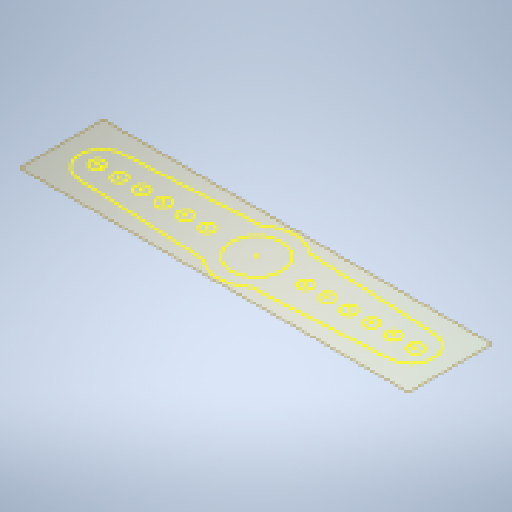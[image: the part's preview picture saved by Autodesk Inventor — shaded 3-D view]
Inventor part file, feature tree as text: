
AUTODESK INVENTOR PART (.ipt)
format: ipt  version: 2024 (Build 280153000, 153)  size: 168,960 bytes
history: native  units: mm
features: other x4, extrude x2, sketch x2, plane x1, reference x1
ambient origin geometry x8: Origin, YZ Plane, XZ Plane, XY Plane, X Axis, Y Axis, Z Axis, Center Point
bodies: Solid1 (feature_tree)
feature tree (10):
  plane  "Work Plane1"
  extrude  "Extrusion1"  Depth=25.0mm
  extrude  "Extrusion2"  Depth=5.0mm
  sketch  "Sketch1"  dims[d0=33.0mm d1=25.0mm]
  reference  "Reference1"
  sketch  "Sketch2"  dims[d2=6.0mm d3=0.0mm d4=5.0mm d5=5.0mm d6=12.9mm d7=12.9mm d8=3.0mm d9=0.0mm]
  other  "<userpath> windows\Documents\Inventor\Robotska_roka\Assembly4.iam"
  other  "Assembly4.iam"
  other  "SG90 - Micro Servo 9g - Tower Pro:2"
  other  "SG90 - Micro Servo 9g - Tower Pro.3"
